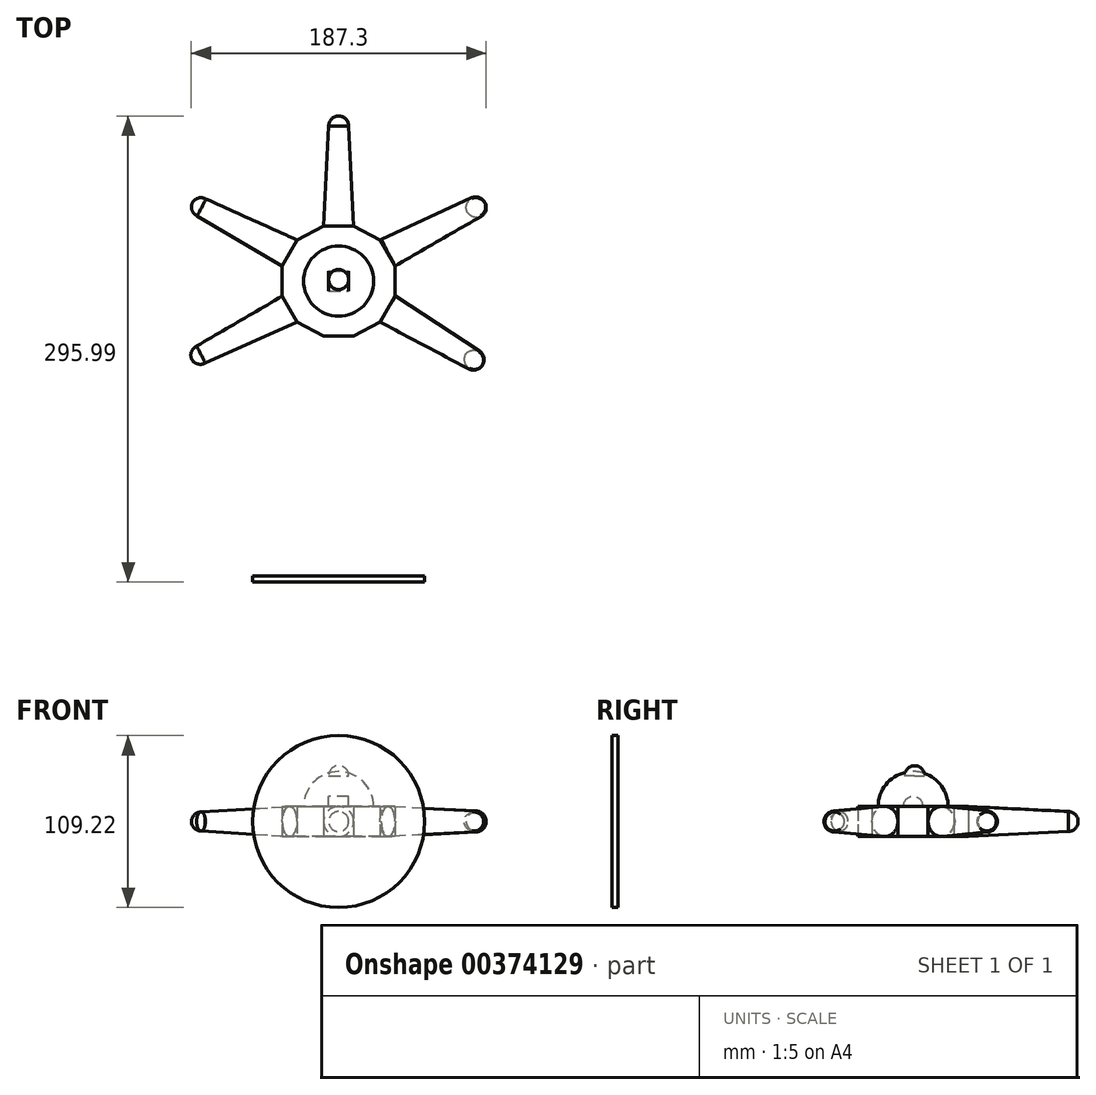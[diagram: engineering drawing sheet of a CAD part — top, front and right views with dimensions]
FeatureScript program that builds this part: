
annotation { "Feature Type Name" : "Feature", "Feature Type Description" : "" }
export const myFeature = defineFeature(function(context is Context, id is Id, definition is map)
    precondition{}
    {
        {
            var Q0;
            Q0=qCreatedBy(makeId("Front.planeOp"),FACE);
            var sketch = newSketch(context, id + "F0", { "sketchPlane" : qUnion([Q0])});
            skLineSegment(sketch, "E0", {"start": v(0, 0) * mm, "end": v(50.8, 0) * mm});
            skLineSegment(sketch, "E1", {"start": v(0, 0) * mm, "end": v(-50.8, 0) * mm});
            skArc(sketch, "E2", {"start": v(50.8, 0) * mm, "mid": v(0, 50.6) * mm, "end": v(-50.8, 0) * mm});
            skCircle(sketch, "E3", {"center": v(0, 0) * mm, "radius": 8.26 * mm});
            skPoint(sketch, "E4", {"position": v(0, 50.6) * mm});
            skArc(sketch, "E5", {"start": v(-50.8, 0) * mm, "mid": v(0, -51.14) * mm, "end": v(50.8, 0) * mm});
            skPoint(sketch, "E6", {"position": v(0, -51.14) * mm});
            skPoint(sketch, "E7", {"position": v(-8.26, 0) * mm});
            skPoint(sketch, "E8", {"position": v(8.26, 0) * mm});
            skPoint(sketch, "E9", {"position": v(0, 8.26) * mm});
            skPoint(sketch, "E10", {"position": v(0, -8.26) * mm});
            skCircle(sketch, "E11", {"center": v(0, 0) * mm, "radius": 10.16 * mm});
            skPoint(sketch, "E12", {"position": v(0, 10.16) * mm});
            skPoint(sketch, "E13", {"position": v(10.16, 0) * mm});
            skPoint(sketch, "E14", {"position": v(0, -10.16) * mm});
            skPoint(sketch, "E15", {"position": v(-10.16, 0) * mm});
            skSolve(sketch);
        }
        {
            var Q0;
            Q0 = qSketchRegion(id + "F0", true);
            var Q1;
            Q1=sQuery(id+"F0.wireOp",EDGE,"E2");
            var Q2;
            Q2=sQuery(id+"F0.wireOp",EDGE,"E1");
            revolve(context, id + "F1", {"bodyType" : ToolBodyType.SURFACE, "entities" : qUnion([Q0]), "surfaceEntities" : qUnion([Q1]), "axis" : qUnion([Q2]), "revolveType" : RevolveType.ONE_DIRECTION, "angle" : 180 * degree});
        }
        {
            var Q0;
            Q0=sQuery(id+"F0.wireOp",EDGE,"E3");
            extrude(context, id + "F2", {"bodyType" : ToolBodyType.SURFACE, "surfaceEntities" : qUnion([Q0]), "endBound" : BoundingType.THROUGH_ALL, "oppositeDirection" : true, "depth" : 25.4 * mm, "hasSecondDirection" : true, "secondDirectionOppositeDirection" : false, "secondDirectionDepth" : 0.25 * mm});
        }
        {
            var Q0;
            Q0=qCreatedBy(makeId("Front.planeOp"),FACE);
            var sketch = newSketch(context, id + "F3", { "sketchPlane" : qUnion([Q0])});
            skCircle(sketch, "E16", {"center": v(0, 0) * mm, "radius": 54.61 * mm});
            skPoint(sketch, "E17", {"position": v(0, 54.61) * mm});
            skPoint(sketch, "E18", {"position": v(0, -54.61) * mm});
            skPoint(sketch, "E19", {"position": v(54.61, 0) * mm});
            skPoint(sketch, "E20", {"position": v(-54.61, 0) * mm});
            skSolve(sketch);
        }
        {
            var Q0;
            Q0 = qSketchRegion(id + "F3", true);
            extrude(context, id + "F4", {"entities" : qUnion([Q0]), "depth" : 3.8 * mm});
        }
        {
            var Q0;
            Q0=sQuery(id+"F0.wireOp",EDGE,"E11");
            extrude(context, id + "F5", {"bodyType" : ToolBodyType.SURFACE, "surfaceEntities" : qUnion([Q0]), "oppositeDirection" : true, "depth" : 53.34 * mm, "hasSecondDirection" : true, "secondDirectionOppositeDirection" : true, "secondDirectionDepth" : 0.25 * mm});
        }
        {
            var Q0;
            Q0=qCreatedBy(makeId("Top.planeOp"),FACE);
            var sketch = newSketch(context, id + "F6", { "sketchPlane" : qUnion([Q0])});
            skLineSegment(sketch, "E21.0", {"start": v(35.83, 196.88) * mm, "end": v(35.83, 177.83) * mm});
            skLineSegment(sketch, "E21.1", {"start": v(35.83, 177.83) * mm, "end": v(26.37, 161.3) * mm});
            skLineSegment(sketch, "E21.2", {"start": v(26.37, 161.3) * mm, "end": v(9.52, 152.4) * mm});
            skLineSegment(sketch, "E21.3", {"start": v(9.53, 152.4) * mm, "end": v(-9.53, 152.4) * mm});
            skLineSegment(sketch, "E21.4", {"start": v(-9.53, 152.4) * mm, "end": v(-26.37, 161.3) * mm});
            skLineSegment(sketch, "E21.5", {"start": v(-26.37, 161.3) * mm, "end": v(-35.83, 177.83) * mm});
            skLineSegment(sketch, "E21.6", {"start": v(-35.83, 177.83) * mm, "end": v(-35.83, 196.88) * mm});
            skLineSegment(sketch, "E21.7", {"start": v(-35.83, 196.88) * mm, "end": v(-26.3, 213.38) * mm});
            skLineSegment(sketch, "E21.8", {"start": v(-26.3, 213.38) * mm, "end": v(-9.53, 222.4) * mm});
            skLineSegment(sketch, "E21.9", {"start": v(-9.53, 222.4) * mm, "end": v(9.52, 222.4) * mm});
            skLineSegment(sketch, "E21.10", {"start": v(9.52, 222.4) * mm, "end": v(26.3, 213.38) * mm});
            skLineSegment(sketch, "E21.11", {"start": v(26.3, 213.38) * mm, "end": v(35.83, 196.88) * mm});
            skPoint(sketch, "E22", {"position": v(0, 152.4) * mm});
            skPoint(sketch, "E23", {"position": v(35.83, 187.36) * mm});
            skPoint(sketch, "E24", {"position": v(-35.83, 187.36) * mm});
            skLineSegment(sketch, "E25", {"start": v(-26.3, 213.38) * mm, "end": v(-84.2, 239.47) * mm});
            skLineSegment(sketch, "E26", {"start": v(-90.55, 228.47) * mm, "end": v(-35.83, 196.88) * mm});
            skPoint(sketch, "E27", {"position": v(-31.06, 205.13) * mm});
            skLineSegment(sketch, "E28", {"start": v(26.3, 213.38) * mm, "end": v(84.2, 239.47) * mm});
            skLineSegment(sketch, "E29", {"start": v(90.55, 228.47) * mm, "end": v(35.83, 196.88) * mm});
            skPoint(sketch, "E30", {"position": v(31.06, 205.13) * mm});
            skPoint(sketch, "E31", {"position": v(-31.1, 169.56) * mm});
            skPoint(sketch, "E32", {"position": v(31.1, 169.56) * mm});
            skLineSegment(sketch, "E33", {"start": v(-9.53, 222.4) * mm, "end": v(-6.35, 285.83) * mm});
            skLineSegment(sketch, "E34", {"start": v(9.52, 222.4) * mm, "end": v(6.35, 285.83) * mm});
            skPoint(sketch, "E35", {"position": v(0, 222.4) * mm});
            skPoint(sketch, "E36", {"position": v(17.95, 156.85) * mm});
            skPoint(sketch, "E37", {"position": v(-17.95, 156.85) * mm});
            skPoint(sketch, "E38", {"position": v(-17.91, 217.9) * mm});
            skPoint(sketch, "E39", {"position": v(17.91, 217.9) * mm});
            skArc(sketch, "E40", {"start": v(-84.2, 239.47) * mm, "mid": v(-92.87, 237.14) * mm, "end": v(-90.55, 228.47) * mm});
            skArc(sketch, "E41", {"start": v(6.35, 285.83) * mm, "mid": v(0, 292.18) * mm, "end": v(-6.35, 285.83) * mm});
            skArc(sketch, "E42", {"start": v(90.55, 228.47) * mm, "mid": v(92.87, 237.14) * mm, "end": v(84.2, 239.47) * mm});
            skLineSegment(sketch, "E43", {"start": v(84.2, 239.47) * mm, "end": v(90.55, 228.47) * mm});
            skLineSegment(sketch, "E44", {"start": v(-90.55, 228.47) * mm, "end": v(-84.2, 239.47) * mm});
            skLineSegment(sketch, "E45", {"start": v(-6.35, 285.83) * mm, "end": v(6.35, 285.83) * mm});
            skLineSegment(sketch, "E46", {"start": v(-35.83, 177.83) * mm, "end": v(-90.95, 146.32) * mm});
            skLineSegment(sketch, "E47", {"start": v(-26.37, 161.3) * mm, "end": v(-84.65, 135.3) * mm});
            skLineSegment(sketch, "E48", {"start": v(26.37, 161.3) * mm, "end": v(82.8, 131.48) * mm});
            skLineSegment(sketch, "E49", {"start": v(35.83, 177.83) * mm, "end": v(88.73, 142.71) * mm});
            skArc(sketch, "E50", {"start": v(82.8, 131.48) * mm, "mid": v(91.38, 134.13) * mm, "end": v(88.73, 142.71) * mm});
            skArc(sketch, "E51", {"start": v(-90.95, 146.32) * mm, "mid": v(-93.31, 137.65) * mm, "end": v(-84.65, 135.3) * mm});
            skLineSegment(sketch, "E52", {"start": v(-90.95, 146.32) * mm, "end": v(-84.65, 135.3) * mm});
            skLineSegment(sketch, "E53", {"start": v(82.8, 131.48) * mm, "end": v(88.73, 142.71) * mm});
            skPoint(sketch, "E54", {"position": v(0, 292.18) * mm});
            skLineSegment(sketch, "E55", {"start": v(0, 292.18) * mm, "end": v(0, 222.4) * mm});
            skPoint(sketch, "E56", {"position": v(-92.87, 237.14) * mm});
            skPoint(sketch, "E57", {"position": v(-93.31, 137.65) * mm});
            skPoint(sketch, "E58", {"position": v(91.38, 134.13) * mm});
            skPoint(sketch, "E59", {"position": v(92.87, 237.14) * mm});
            skLineSegment(sketch, "E60", {"start": v(31.06, 205.13) * mm, "end": v(92.87, 237.14) * mm});
            skLineSegment(sketch, "E61", {"start": v(-92.87, 237.14) * mm, "end": v(-31.06, 205.13) * mm});
            skLineSegment(sketch, "E62", {"start": v(-31.1, 169.56) * mm, "end": v(-93.31, 137.65) * mm});
            skLineSegment(sketch, "E63", {"start": v(31.1, 169.56) * mm, "end": v(91.38, 134.13) * mm});
            skPoint(sketch, "E64", {"position": v(0, 187.38) * mm});
            skCircle(sketch, "E65", {"center": v(0, 187.38) * mm, "radius": 20.96 * mm});
            skPoint(sketch, "E66", {"position": v(0, 208.34) * mm});
            skPoint(sketch, "E67", {"position": v(0, 166.43) * mm});
            skPoint(sketch, "E68", {"position": v(20.96, 187.38) * mm});
            skPoint(sketch, "E69", {"position": v(-20.95, 187.36) * mm});
            skSolve(sketch);
        }
        {
            var Q0;
            Q0=makeQuery(id+"F6.imprint","IMPRINT",FACE,{"disambiguationData":[TD([[makeQuery(id+"F6.imprint","IMPRINT",EDGE,{"derivedFrom":sQuery(id+"F6.wireOp",EDGE,"E21.0")}),-1.0]])]});
            var Q1;
            Q1=makeQuery(id+"F6.imprint","IMPRINT",FACE,{"disambiguationData":[TD([[makeQuery(id+"F6.imprint","IMPRINT",EDGE,{"derivedFrom":sQuery(id+"F6.wireOp",EDGE,"mh1GqOM7-qSFT-ApzD-fGjL-p0bSeOK2bNAU")}),1.0]])]});
            var Q2;
            Q2=makeQuery(id+"F6.imprint","IMPRINT",FACE,{"disambiguationData":[TD([[makeQuery(id+"F6.imprint","IMPRINT",EDGE,{"derivedFrom":sQuery(id+"F6.wireOp",EDGE,"E65")}),1.0]])]});
            extrude(context, id + "F7", {"entities" : qUnion([Q0, Q1, Q2]), "depth" : 9.52 * mm, "hasSecondDirection" : true, "secondDirectionOppositeDirection" : true, "secondDirectionDepth" : 9.52 * mm});
        }
        {
            var Q0;
            Q0=qCreatedBy(makeId("Top.planeOp"),FACE);
            var sketch = newSketch(context, id + "F8", { "sketchPlane" : qUnion([Q0])});
            skPoint(sketch, "E70", {"position": v(-9.53, 152.4) * mm});
            skPoint(sketch, "E71", {"position": v(9.53, 152.4) * mm});
            skPoint(sketch, "E72", {"position": v(0, 173.57) * mm});
            skPoint(sketch, "E73", {"position": v(0, 129.7) * mm});
            skLineSegment(sketch, "E74", {"start": v(0, 129.7) * mm, "end": v(0, 0) * mm});
            skLineSegment(sketch, "E75", {"start": v(9.52, 152.4) * mm, "end": v(-9.53, 152.4) * mm});
            skArc(sketch, "E76", {"start": v(0, 129.7) * mm, "mid": v(8.47, 139.5) * mm, "end": v(9.53, 152.4) * mm});
            skPoint(sketch, "E77", {"position": v(0, 152.4) * mm});
            skSolve(sketch);
        }
        {
            var Q0;
            Q0=sQuery(id+"F8.wireOp",EDGE,"E76");
            var Q1;
            Q1=sQuery(id+"F8.wireOp",EDGE,"E74");
            revolve(context, id + "F9", {"bodyType" : ToolBodyType.SURFACE, "surfaceEntities" : qUnion([Q0]), "axis" : qUnion([Q1]), "revolveType" : RevolveType.FULL});
        }
        {
            var Q0;
            {var subQ0=sQuery(id+"F6.wireOp",EDGE,"E34");Q0=makeQuery(id+"F6.imprint","IMPRINT",FACE,{"disambiguationData":[TD([[makeQuery(id+"F6.imprint","IMPRINT",EDGE,{"derivedFrom":subQ0}),1.0]])]});}
            var Q1;
            {var subQ1=sQuery(id+"F6.wireOp",EDGE,"E41");var subQ3=sQuery(id+"F6.wireOp",EDGE,"E55");var subQ4=makeQuery(id+"F6.imprint","INTERSECT",VERTEX,{"derivedFrom":[subQ1,subQ3]});Q1=makeQuery(id+"F6.imprint","IMPRINT",FACE,{"disambiguationData":[TD([[makeQuery(id+"F6.imprint","IMPRINT",EDGE,{"disambiguationData":[TD([[subQ4,-1.0]])],"derivedFrom":subQ3}),1.0]])]});}
            var Q2;
            Q2=sQuery(id+"F6.wireOp",EDGE,"E34");
            var Q3;
            Q3=sQuery(id+"F6.wireOp",EDGE,"E41");
            var Q4;
            Q4=sQuery(id+"F6.wireOp",EDGE,"E33");
            var Q5;
            Q5=sQuery(id+"F6.wireOp",EDGE,"E55");
            revolve(context, id + "F10", {"operationType" : NewBodyOperationType.ADD, "entities" : qUnion([Q0, Q1]), "surfaceEntities" : qUnion([Q2, Q3, Q4]), "axis" : qUnion([Q5]), "revolveType" : RevolveType.FULL});
        }
        {
            var Q0;
            {var subQ0=sQuery(id+"F6.wireOp",EDGE,"E25");Q0=makeQuery(id+"F6.imprint","IMPRINT",FACE,{"disambiguationData":[TD([[makeQuery(id+"F6.imprint","IMPRINT",EDGE,{"derivedFrom":subQ0}),1.0]])]});}
            var Q1;
            {var subQ1=sQuery(id+"F6.wireOp",EDGE,"E40");var subQ3=sQuery(id+"F6.wireOp",EDGE,"E61");var subQ4=makeQuery(id+"F6.imprint","INTERSECT",VERTEX,{"derivedFrom":[subQ1,subQ3]});Q1=makeQuery(id+"F6.imprint","IMPRINT",FACE,{"disambiguationData":[TD([[makeQuery(id+"F6.imprint","IMPRINT",EDGE,{"disambiguationData":[TD([[subQ4,-1.0]])],"derivedFrom":subQ3}),1.0]])]});}
            var Q2;
            Q2=sQuery(id+"F6.wireOp",EDGE,"E61");
            revolve(context, id + "F11", {"operationType" : NewBodyOperationType.ADD, "entities" : qUnion([Q0, Q1]), "axis" : qUnion([Q2]), "revolveType" : RevolveType.FULL});
        }
        {
            var Q0;
            {var subQ0=sQuery(id+"F6.wireOp",EDGE,"E29");Q0=makeQuery(id+"F6.imprint","IMPRINT",FACE,{"disambiguationData":[TD([[makeQuery(id+"F6.imprint","IMPRINT",EDGE,{"derivedFrom":subQ0}),-1.0]])]});}
            var Q1;
            {var subQ1=sQuery(id+"F6.wireOp",EDGE,"E42");var subQ3=sQuery(id+"F6.wireOp",EDGE,"E60");var subQ4=makeQuery(id+"F6.imprint","INTERSECT",VERTEX,{"derivedFrom":[subQ1,subQ3]});Q1=makeQuery(id+"F6.imprint","IMPRINT",FACE,{"disambiguationData":[TD([[makeQuery(id+"F6.imprint","IMPRINT",EDGE,{"disambiguationData":[TD([[subQ4,1.0]])],"derivedFrom":subQ3}),-1.0]])]});}
            var Q2;
            Q2=sQuery(id+"F6.wireOp",EDGE,"E60");
            revolve(context, id + "F12", {"operationType" : NewBodyOperationType.ADD, "entities" : qUnion([Q0, Q1]), "axis" : qUnion([Q2]), "revolveType" : RevolveType.FULL});
        }
        {
            var Q0;
            {var subQ0=sQuery(id+"F6.wireOp",EDGE,"E47");Q0=makeQuery(id+"F6.imprint","IMPRINT",FACE,{"disambiguationData":[TD([[makeQuery(id+"F6.imprint","IMPRINT",EDGE,{"derivedFrom":subQ0}),-1.0]])]});}
            var Q1;
            {var subQ1=sQuery(id+"F6.wireOp",EDGE,"E51");var subQ3=sQuery(id+"F6.wireOp",EDGE,"E62");var subQ4=makeQuery(id+"F6.imprint","INTERSECT",VERTEX,{"derivedFrom":[subQ1,subQ3]});Q1=makeQuery(id+"F6.imprint","IMPRINT",FACE,{"disambiguationData":[TD([[makeQuery(id+"F6.imprint","IMPRINT",EDGE,{"disambiguationData":[TD([[subQ4,1.0]])],"derivedFrom":subQ3}),1.0]])]});}
            var Q2;
            Q2=sQuery(id+"F6.wireOp",EDGE,"E62");
            revolve(context, id + "F13", {"operationType" : NewBodyOperationType.ADD, "entities" : qUnion([Q0, Q1]), "axis" : qUnion([Q2]), "revolveType" : RevolveType.FULL});
        }
        {
            var Q0;
            {var subQ0=sQuery(id+"F6.wireOp",EDGE,"E48");Q0=makeQuery(id+"F6.imprint","IMPRINT",FACE,{"disambiguationData":[TD([[makeQuery(id+"F6.imprint","IMPRINT",EDGE,{"derivedFrom":subQ0}),1.0]])]});}
            var Q1;
            {var subQ1=sQuery(id+"F6.wireOp",EDGE,"E50");var subQ3=sQuery(id+"F6.wireOp",EDGE,"E63");var subQ4=makeQuery(id+"F6.imprint","INTERSECT",VERTEX,{"derivedFrom":[subQ1,subQ3]});Q1=makeQuery(id+"F6.imprint","IMPRINT",FACE,{"disambiguationData":[TD([[makeQuery(id+"F6.imprint","IMPRINT",EDGE,{"disambiguationData":[TD([[subQ4,1.0]])],"derivedFrom":subQ3}),-1.0]])]});}
            var Q2;
            Q2=sQuery(id+"F6.wireOp",EDGE,"E63");
            revolve(context, id + "F14", {"operationType" : NewBodyOperationType.ADD, "entities" : qUnion([Q0, Q1]), "axis" : qUnion([Q2]), "revolveType" : RevolveType.FULL});
        }
        {
            var Q0;
            Q0=makeQuery(id+"F7.opExtrude","CAP_FACE",FACE,{"disambiguationData":[OSD([sQuery(id+"F6.wireOp",EDGE,"E21.0"),sQuery(id+"F6.wireOp",EDGE,"E21.1"),sQuery(id+"F6.wireOp",EDGE,"E21.2"),sQuery(id+"F6.wireOp",EDGE,"E21.3"),sQuery(id+"F6.wireOp",EDGE,"E21.4"),sQuery(id+"F6.wireOp",EDGE,"E21.5"),sQuery(id+"F6.wireOp",EDGE,"E21.6"),sQuery(id+"F6.wireOp",EDGE,"E21.7"),sQuery(id+"F6.wireOp",EDGE,"E21.8"),sQuery(id+"F6.wireOp",EDGE,"E21.9"),sQuery(id+"F6.wireOp",EDGE,"E21.10"),sQuery(id+"F6.wireOp",EDGE,"E21.11")])],"isStart":false});
            var sketch = newSketch(context, id + "F15", { "sketchPlane" : qUnion([Q0])});
            skCircle(sketch, "E78", {"center": v(0, 187.36) * mm, "radius": 22.23 * mm});
            skPoint(sketch, "E78.centerSnap0", {"position": v(-35.83, 187.36) * mm});
            skPoint(sketch, "E79", {"position": v(-22.23, 187.36) * mm});
            skPoint(sketch, "E80", {"position": v(22.23, 187.36) * mm});
            skPoint(sketch, "E80.positionSnap0", {"position": v(35.83, 187.36) * mm});
            skLineSegment(sketch, "E81", {"start": v(-22.23, 187.36) * mm, "end": v(22.23, 187.36) * mm});
            skLineSegment(sketch, "E82", {"start": v(0, 193.7) * mm, "end": v(6.35, 193.7) * mm});
            skLineSegment(sketch, "E83", {"start": v(6.35, 193.7) * mm, "end": v(6.35, 187.36) * mm});
            skLineSegment(sketch, "E84", {"start": v(0, 193.7) * mm, "end": v(-6.35, 193.7) * mm});
            skLineSegment(sketch, "E85", {"start": v(-6.35, 193.7) * mm, "end": v(-6.35, 187.36) * mm});
            skLineSegment(sketch, "E86", {"start": v(-6.35, 187.36) * mm, "end": v(-6.35, 181) * mm});
            skLineSegment(sketch, "E87", {"start": v(-6.35, 181) * mm, "end": v(0, 181) * mm});
            skLineSegment(sketch, "E88", {"start": v(0, 181) * mm, "end": v(6.35, 181) * mm});
            skLineSegment(sketch, "E89", {"start": v(6.35, 181) * mm, "end": v(6.35, 187.36) * mm});
            skSolve(sketch);
        }
        {
            var Q0;
            {var subQ0=sQuery(id+"F15.wireOp",EDGE,"E81");Q0=makeQuery(id+"F15.imprint","IMPRINT",FACE,{"disambiguationData":[TD([[makeQuery(id+"F15.imprint","IMPRINT",EDGE,{"derivedFrom":subQ0}),1.0]])]});}
            var Q1;
            Q1=sQuery(id+"F15.wireOp",EDGE,"E78");
            var Q2;
            Q2=sQuery(id+"F15.wireOp",EDGE,"E81");
            revolve(context, id + "F16", {"entities" : qUnion([Q0]), "surfaceEntities" : qUnion([Q1]), "axis" : qUnion([Q2]), "revolveType" : RevolveType.ONE_DIRECTION, "angle" : 180 * degree});
        }
        {
            var Q0;
            Q0=sQuery(id+"F15.wireOp",EDGE,"E85");
            var Q1;
            Q1=sQuery(id+"F15.wireOp",EDGE,"E84");
            var Q2;
            Q2=sQuery(id+"F15.wireOp",EDGE,"E82");
            var Q3;
            Q3=sQuery(id+"F15.wireOp",EDGE,"E83");
            var Q4;
            Q4=sQuery(id+"F15.wireOp",EDGE,"E89");
            var Q5;
            Q5=sQuery(id+"F15.wireOp",EDGE,"E88");
            var Q6;
            Q6=sQuery(id+"F15.wireOp",EDGE,"E87");
            var Q7;
            Q7=sQuery(id+"F15.wireOp",EDGE,"E86");
            extrude(context, id + "F17", {"bodyType" : ToolBodyType.SURFACE, "surfaceEntities" : qUnion([Q0, Q1, Q2, Q3, Q4, Q5, Q6, Q7]), "depth" : 19.56 * mm});
        }
        {
            var Q0;
            Q0=makeQuery(id+"F17.opExtrude","CAP_EDGE",EDGE,{"disambiguationData":[OSD([sQuery(id+"F15.wireOp",EDGE,"E85"),sQuery(id+"F15.wireOp",EDGE,"E86")])],"isStart":false});
            cPlane(context, id + "F18", {"entities" : qUnion([Q0]), "cplaneType" : CPlaneType.LINE_ANGLE, "offset" : 25.4 * mm, "angle" : 180 * degree, "oppositeDirection" : true, "width" : 152.4 * mm, "height" : 152.4 * mm});
        }
        {
            var Q0;
            Q0=qCreatedBy(id+"F18.planeOp",FACE);
            var sketch = newSketch(context, id + "F19", { "sketchPlane" : qUnion([Q0])});
            skCircle(sketch, "E90", {"center": v(0, 188.3) * mm, "radius": 6.35 * mm});
            skPoint(sketch, "E91", {"position": v(-6.35, 188.3) * mm});
            skPoint(sketch, "E92", {"position": v(6.35, 188.3) * mm});
            skLineSegment(sketch, "E93", {"start": v(-6.35, 188.3) * mm, "end": v(6.35, 188.3) * mm});
            skSolve(sketch);
        }
        {
            var Q0;
            {var subQ0=sQuery(id+"F19.wireOp",EDGE,"E93");Q0=makeQuery(id+"F19.imprint","IMPRINT",FACE,{"disambiguationData":[TD([[makeQuery(id+"F19.imprint","IMPRINT",EDGE,{"derivedFrom":subQ0}),-1.0]])]});}
            var Q1;
            Q1=sQuery(id+"F19.wireOp",EDGE,"E90");
            var Q2;
            Q2=sQuery(id+"F19.wireOp",EDGE,"E93");
            revolve(context, id + "F20", {"entities" : qUnion([Q0]), "surfaceEntities" : qUnion([Q1]), "axis" : qUnion([Q2]), "revolveType" : RevolveType.ONE_DIRECTION, "oppositeDirection" : true, "angle" : 180 * degree});
        }
        {
            var Q0;
            Q0=makeQuery(id+"F9.opRevolve","SWEPT_FACE",FACE,{"disambiguationData":[OSD([sQuery(id+"F8.wireOp",EDGE,"E76")])]});
            cPlane(context, id + "F21", {"entities" : qUnion([Q0]), "cplaneType" : CPlaneType.LINE_ANGLE, "offset" : 25.4 * mm, "angle" : 180 * degree, "oppositeDirection" : true, "width" : 152.4 * mm, "height" : 152.4 * mm});
        }
        {
            var Q0;
            Q0=qCreatedBy(id+"F21.planeOp",FACE);
            var sketch = newSketch(context, id + "F22", { "sketchPlane" : qUnion([Q0])});
            skCircle(sketch, "E94", {"center": v(0, 146.29) * mm, "radius": 2.35 * mm});
            skSolve(sketch);
        }
        {
            var Q0;
            Q0=sQuery(id+"F22.wireOp",EDGE,"E94");
            extrude(context, id + "F23", {"bodyType" : ToolBodyType.SURFACE, "surfaceEntities" : qUnion([Q0]), "depth" : 50.8 * mm});
        }
    });
